# Revit family: IS_Connect_N1383_BIM_DE
name_source: partatom
category: Plumbing Fixtures
revit_build: Autodesk Revit MEP 2016 (Build: 20161004_0715(x64)
units: mm (PartAtom-declared; Revit-internal decimal feet)

## family parameters
Always vertical = No
Cut with Voids When Loaded = No
OmniClass Number = 23.45.05.14.21.11
OmniClass Title = Bath/Shower Units
Part Type = Normal
Room Calculation Point = No
Round Connector Dimension = Use Diameter
Shared = No
Work Plane-Based = No

## types (1)
- N1383AA CONNECT spare toilet roll holder
    AreaUnits = millimeters
    AssetType = Fixed
    BIMObjectName = ISI_IdealStandard_Furniture_Connect_E1383AA
    BIMobject category = Accessories
    BOSUseNativeGeometries = 1
    Brand url = http://www.idealstandard.co.uk
    ConnectionType = Mechanical
    CurrencyUnit = €
    Date of publishing = 06/11/2017
    DurationUnit = year
    EAN code = https://8014140353683
    Edition number = 1
    IFC Classification = Sanitary Terminal
    IfcExportAs = Sanitary Terminal Type
    IfcExportType = ToiletRollHolders
    Installation instructions = http://www.idealstandard.de
    LinearUnits = millimeters
    Manufacturer name = Ideal Standard
    Model = E1383AA
    NBS Reference Code = 35-75-88
    NBS Reference Description = Toilet Roll Holders
    Name = Furniture_Connect_E1383AA_IdealStandard
    Nominal height = 151
    Nominal width = 25
    NominalDepth = 89 mm  [stored 0.291995 ft]
    NominalHeight = 25 mm  [stored 0.082021 ft]
    NominalLength = 89 mm  [stored 0.291995 ft]
    NominalWidth = 151 mm  [stored 0.495407 ft]
    OmniClass Code = 23-31 25 00
    OmniClass Description = Toilet and Bath Specialties
    Product Guid = 6fb48db3-7073-4701-a440-93b057779d96
    Product SKU = N1383
    Product data url = https://bimobject.com
    Product family = CONNECT
    Product group = Accessories
    Product name = CONNECT spare toilet roll holder
    Product url = http://www.idealstandard.de
    QR code = http://bimobject.com
    Size = 151x89x25 mm
    Space = Internal
    Technical description = http://www.idealstandard.de
    Uniclass 1.4 Code = L7313
    Uniclass 1.4 Description = Sanitary above ground pipes and fittings
    Uniclass 2.0 Code = PR-35-75-88
    Uniclass 2.0 Description = Toilet Roll Holders
    Uniclass 2015 Code = Pr_40_20_76_88
    Uniclass 2015 Name = Toilet roll holders
    Uniclass2015Code = Pr_40_20_76_88
    Uniclass2015Title = Toilet roll holders
    Uniclass2015Version = Products v1.1
    Version = 1
    Weight Net (Kg) = 0.55

note: [stored X ft] marks values corroborated as IEEE doubles in the binary element streams (Revit-internal decimal feet)

## geometry (parser evidence)
native form markers: Blend x4, Sweep x1
no freeform markers — native parametric forms only
